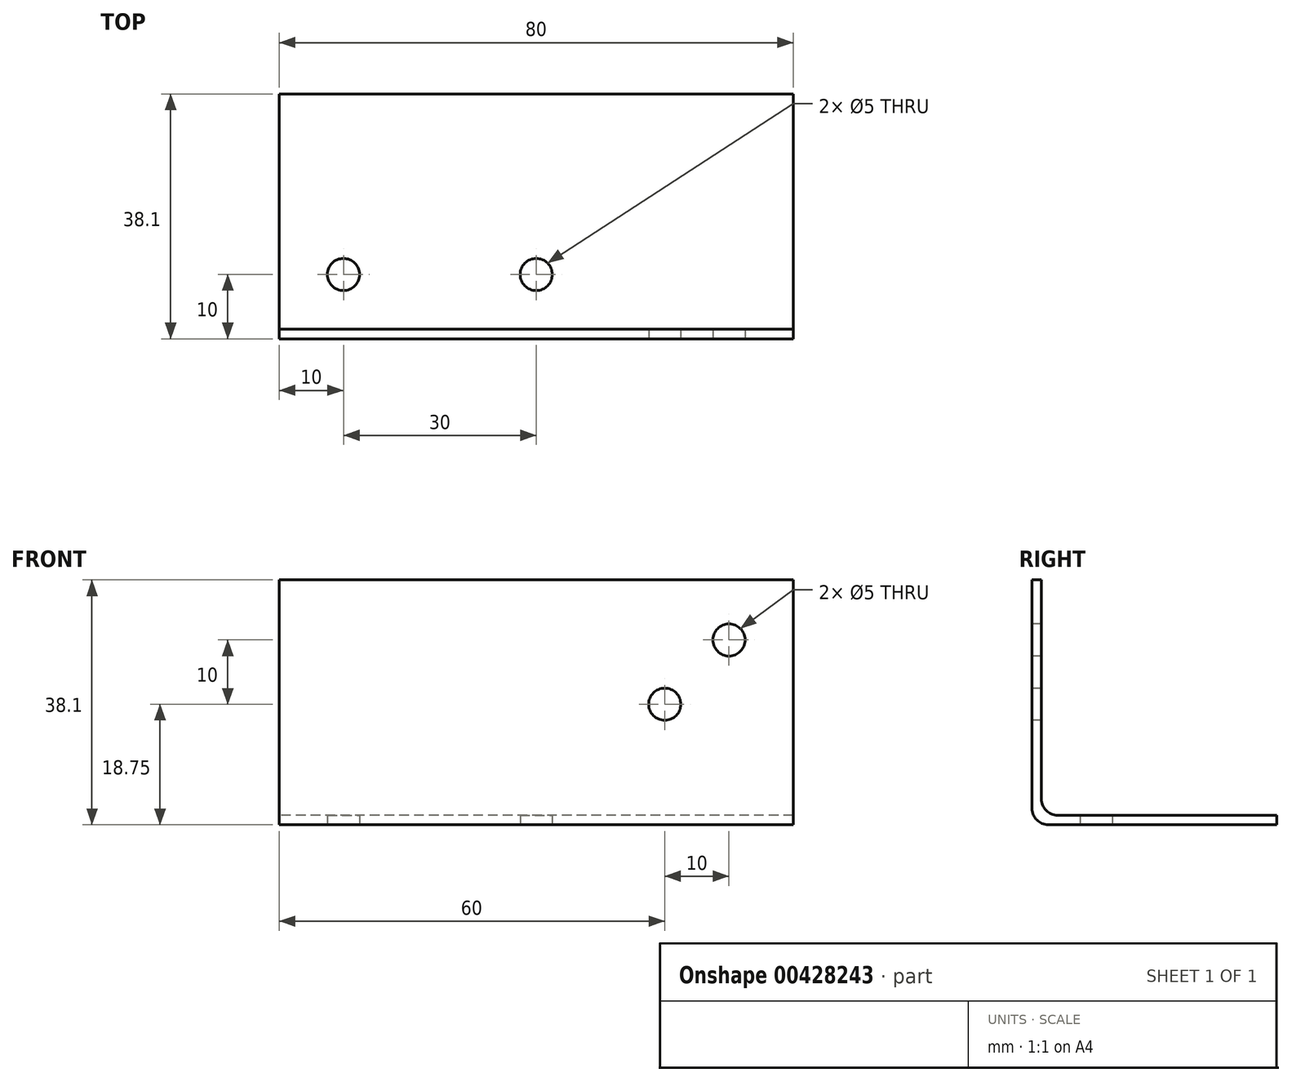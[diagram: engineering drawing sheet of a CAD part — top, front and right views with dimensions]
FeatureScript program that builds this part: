
annotation { "Feature Type Name" : "Feature", "Feature Type Description" : "" }
export const myFeature = defineFeature(function(context is Context, id is Id, definition is map)
    precondition{}
    {
        {
            var Q0;
            Q0=qCreatedBy(makeId("Right.planeOp"),FACE);
            var sketch = newSketch(context, id + "F0", { "sketchPlane" : qUnion([Q0])});
            skLineSegment(sketch, "E0.bottom", {"start": v(0, 0) * mm, "end": v(0, 0) * mm});
            skLineSegment(sketch, "E1", {"start": v(0, 0) * mm, "end": v(38.1, 0) * mm, "construction": true});
            skLineSegment(sketch, "E2", {"start": v(38.1, 0) * mm, "end": v(38.1, 1.47) * mm, "construction": true});
            skLineSegment(sketch, "E3", {"start": v(38.1, 1.47) * mm, "end": v(1.47, 1.47) * mm, "construction": true});
            skLineSegment(sketch, "E4", {"start": v(1.47, 1.47) * mm, "end": v(1.47, 38.1) * mm, "construction": true});
            skLineSegment(sketch, "E5", {"start": v(1.47, 38.1) * mm, "end": v(0, 38.1) * mm, "construction": true});
            skLineSegment(sketch, "E6", {"start": v(0, 38.1) * mm, "end": v(0, 0) * mm, "construction": true});
            skLineSegment(sketch, "E7", {"start": v(0, 38.1) * mm, "end": v(0, 2.54) * mm});
            skLineSegment(sketch, "E8", {"start": v(2.54, 0) * mm, "end": v(38.1, 0) * mm});
            skLineSegment(sketch, "E9", {"start": v(38.1, 0) * mm, "end": v(38.1, 1.47) * mm});
            skLineSegment(sketch, "E10", {"start": v(38.1, 1.47) * mm, "end": v(4.01, 1.47) * mm});
            skLineSegment(sketch, "E11", {"start": v(1.47, 4.01) * mm, "end": v(1.47, 38.1) * mm});
            skLineSegment(sketch, "E12", {"start": v(1.47, 38.1) * mm, "end": v(0, 38.1) * mm});
            skPoint(sketch, "E13.visualSharp", {"position": v(1.47, 1.47) * mm});
            skArc(sketch, "E13.filletArc", {"start": v(1.47, 4.01) * mm, "mid": v(2.22, 2.22) * mm, "end": v(4.01, 1.47) * mm});
            skPoint(sketch, "E14.visualSharp", {"position": v(0, 0) * mm});
            skArc(sketch, "E14.filletArc", {"start": v(0, 2.54) * mm, "mid": v(0.74, 0.74) * mm, "end": v(2.54, 0) * mm});
            skSolve(sketch);
        }
        {
            var Q0;
            Q0=makeQuery(id+"F0.imprint","IMPRINT",FACE,{"disambiguationData":[TD([[makeQuery(id+"F0.imprint","IMPRINT",EDGE,{"derivedFrom":sQuery(id+"F0.wireOp",EDGE,"E7")}),1.0]])]});
            extrude(context, id + "F1", {"entities" : qUnion([Q0]), "depth" : 80 * mm, "offsetDistance" : 25.4 * mm, "symmetric" : true});
        }
        {
            var Q0;
            Q0=qCreatedBy(makeId("Top.planeOp"),FACE);
            var sketch = newSketch(context, id + "F2", { "sketchPlane" : qUnion([Q0])});
            skLineSegment(sketch, "E15", {"start": v(-50.07, 10) * mm, "end": v(52.33, 10) * mm, "construction": true});
            skCircle(sketch, "E16", {"center": v(-30, 10) * mm, "radius": 2.5 * mm});
            skLineSegment(sketch, "E17", {"start": v(0, 0) * mm, "end": v(0, 46.38) * mm, "construction": true});
            skCircle(sketch, "E18.MirrorC", {"center": v(30, 10) * mm, "radius": 2.5 * mm});
            skCircle(sketch, "E19", {"center": v(0, 10) * mm, "radius": 2.5 * mm});
            skSolve(sketch);
        }
        {
            var Q0;
            Q0=makeQuery(id+"F2.imprint","IMPRINT",FACE,{"disambiguationData":[TD([[makeQuery(id+"F2.imprint","IMPRINT",EDGE,{"derivedFrom":sQuery(id+"F2.wireOp",EDGE,"E16")}),1.0]])]});
            var Q1;
            Q1=makeQuery(id+"F2.imprint","IMPRINT",FACE,{"disambiguationData":[TD([[makeQuery(id+"F2.imprint","IMPRINT",EDGE,{"derivedFrom":sQuery(id+"F2.wireOp",EDGE,"E19")}),1.0]])]});
            var Q2;
            Q2=makeQuery(id+"F2.imprint","IMPRINT",FACE,{"disambiguationData":[TD([[makeQuery(id+"F2.imprint","IMPRINT",EDGE,{"derivedFrom":sQuery(id+"F2.wireOp",EDGE,"E18.MirrorC")}),-1.0]])]});
            var Q3;
            Q3=sQuery(id+"F2.wireOp",EDGE,"Vt0wxe4o-B6rk-JuP7-bmht-X0GgRwPQRYbh");
            var Q4;
            Q4=sQuery(id+"F2.wireOp",EDGE,"7a2bea94-8bb3-4732-811a-091233b52b460.MirrorC");
            var Q5;
            Q5=sQuery(id+"F2.wireOp",EDGE,"E18.MirrorC");
            var Q6;
            Q6=sQuery(id+"F2.wireOp",EDGE,"E16");
            extrude(context, id + "F3", {"entities" : qUnion([Q0, Q1, Q2]), "operationType" : NewBodyOperationType.REMOVE, "surfaceEntities" : qUnion([Q3, Q4, Q5, Q6]), "depth" : 25.4 * mm, "offsetDistance" : 25.4 * mm, "symmetric" : true});
        }
        {
            var Q0;
            Q0=qCreatedBy(makeId("Front.planeOp"),FACE);
            var sketch = newSketch(context, id + "F4", { "sketchPlane" : qUnion([Q0])});
            skLineSegment(sketch, "E20", {"start": v(0, 0) * mm, "end": v(0, 176.44) * mm, "construction": true});
            skLineSegment(sketch, "E21", {"start": v(233.74, 28.75) * mm, "end": v(-238.1, 28.75) * mm, "construction": true});
            skLineSegment(sketch, "E22", {"start": v(30, 44.85) * mm, "end": v(30, -13.55) * mm, "construction": true});
            skCircle(sketch, "E23", {"center": v(30, 28.75) * mm, "radius": 2.5 * mm});
            skCircle(sketch, "E24.MirrorC", {"center": v(-30, 28.75) * mm, "radius": 2.5 * mm});
            skLineSegment(sketch, "E25", {"start": v(47.27, 18.75) * mm, "end": v(-45.55, 18.75) * mm, "construction": true});
            skLineSegment(sketch, "E26", {"start": v(20, 40.95) * mm, "end": v(20, -13.28) * mm, "construction": true});
            skCircle(sketch, "E27", {"center": v(20, 18.75) * mm, "radius": 2.5 * mm});
            skCircle(sketch, "E28.MirrorC", {"center": v(-20, 18.75) * mm, "radius": 2.5 * mm});
            skSolve(sketch);
        }
        {
            var Q0;
            Q0=makeQuery(id+"F4.imprint","IMPRINT",FACE,{"disambiguationData":[TD([[makeQuery(id+"F4.imprint","IMPRINT",EDGE,{"derivedFrom":sQuery(id+"F4.wireOp",EDGE,"E24.MirrorC")}),-1.0]])]});
            var Q1;
            Q1=makeQuery(id+"F4.imprint","IMPRINT",FACE,{"disambiguationData":[TD([[makeQuery(id+"F4.imprint","IMPRINT",EDGE,{"derivedFrom":sQuery(id+"F4.wireOp",EDGE,"E23")}),1.0]])]});
            var Q2;
            Q2=makeQuery(id+"F4.imprint","IMPRINT",FACE,{"disambiguationData":[TD([[makeQuery(id+"F4.imprint","IMPRINT",EDGE,{"derivedFrom":sQuery(id+"F4.wireOp",EDGE,"E27")}),1.0]])]});
            var Q3;
            Q3=makeQuery(id+"F4.imprint","IMPRINT",FACE,{"disambiguationData":[TD([[makeQuery(id+"F4.imprint","IMPRINT",EDGE,{"derivedFrom":sQuery(id+"F4.wireOp",EDGE,"E28.MirrorC")}),-1.0]])]});
            var Q4;
            Q4=sQuery(id+"F4.wireOp",EDGE,"E23");
            extrude(context, id + "F5", {"entities" : qUnion([Q0, Q1, Q2, Q3]), "operationType" : NewBodyOperationType.REMOVE, "surfaceEntities" : qUnion([Q4]), "oppositeDirection" : true, "depth" : 25.4 * mm, "offsetDistance" : 25.4 * mm, "symmetric" : true});
        }
    });
